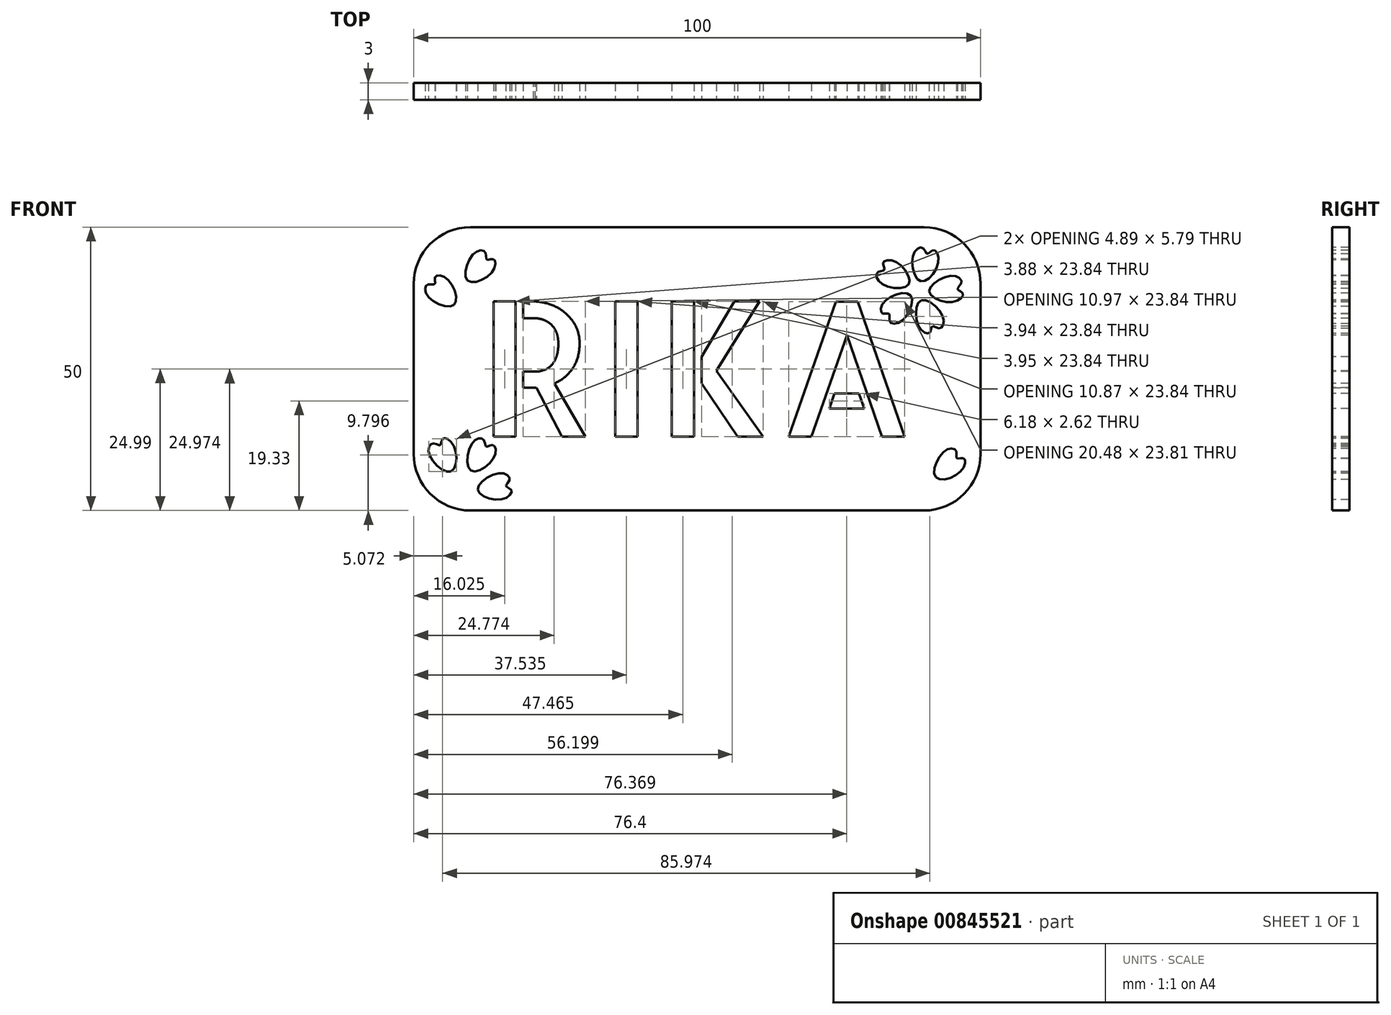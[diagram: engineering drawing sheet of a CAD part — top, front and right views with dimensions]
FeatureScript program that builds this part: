
annotation { "Feature Type Name" : "Feature", "Feature Type Description" : "" }
export const myFeature = defineFeature(function(context is Context, id is Id, definition is map)
    precondition{}
    {
        {
            var Q0;
            Q0=qCreatedBy(makeId("Front.planeOp"),FACE);
            var sketch = newSketch(context, id + "F0", { "sketchPlane" : qUnion([Q0])});
            skLineSegment(sketch, "E0.bottom", {"start": v(-50, 50) * mm, "end": v(50, 50) * mm});
            skLineSegment(sketch, "E0.top", {"start": v(-50, 0) * mm, "end": v(50, 0) * mm});
            skLineSegment(sketch, "E0.left", {"start": v(-50, 50) * mm, "end": v(-50, 0) * mm});
            skLineSegment(sketch, "E0.right", {"start": v(50, 50) * mm, "end": v(50, 0) * mm});
            skPoint(sketch, "E1", {"position": v(0, 0) * mm});
            skSolve(sketch);
        }
        {
            var Q0;
            Q0=qSketchRegion(id+"F0",true);
            extrude(context, id + "F1", {"entities" : qUnion([Q0]), "endBound" : BoundingType.SYMMETRIC, "depth" : 3 * mm, "offsetDistance" : 25 * mm});
        }
        {
            var Q0;
            Q0=makeQuery(id+"F1.opExtrude","SWEPT_EDGE",EDGE,{"disambiguationData":[OSD([sQuery(id+"F0.wireOp",EDGE,"E0.bottom"),sQuery(id+"F0.wireOp",EDGE,"E0.left")])]});
            var Q1;
            Q1=makeQuery(id+"F1.opExtrude","SWEPT_EDGE",EDGE,{"disambiguationData":[OSD([sQuery(id+"F0.wireOp",EDGE,"E0.bottom"),sQuery(id+"F0.wireOp",EDGE,"E0.right")])]});
            var Q2;
            Q2=makeQuery(id+"F1.opExtrude","SWEPT_EDGE",EDGE,{"disambiguationData":[OSD([sQuery(id+"F0.wireOp",EDGE,"E0.top"),sQuery(id+"F0.wireOp",EDGE,"E0.right")])]});
            var Q3;
            Q3=makeQuery(id+"F1.opExtrude","SWEPT_EDGE",EDGE,{"disambiguationData":[OSD([sQuery(id+"F0.wireOp",EDGE,"E0.top"),sQuery(id+"F0.wireOp",EDGE,"E0.left")])]});
            fillet(context, id + "F2", {"entities" : qUnion([Q0, Q1, Q2, Q3]), "radius" : 10 * mm, "tangentPropagation" : true, "allowEdgeOverflow" : false});
        }
        {
            var Q0;
            Q0=makeQuery(id+"F1.opExtrude","CAP_FACE",FACE,{"disambiguationData":[OSD([sQuery(id+"F0.wireOp",EDGE,"E0.bottom"),sQuery(id+"F0.wireOp",EDGE,"E0.top"),sQuery(id+"F0.wireOp",EDGE,"E0.left"),sQuery(id+"F0.wireOp",EDGE,"E0.right")])],"isStart":false});
            var sketch = newSketch(context, id + "F3", { "sketchPlane" : qUnion([Q0])});
            skText(sketch, "E2", { "text": "RIKA", "fontName": "AllertaStencil-Regular.ttf"});
            skPoint(sketch, "E3", {"position": v(-38.83, 25) * mm});
            const initialGuessF3  = {"E2": [-0.03883, 0.01307, 1, 0, 0.02385]};
            skSetInitialGuess(sketch, initialGuessF3);
            skSolve(sketch);
        }
        {
            var Q0;
            Q0=qSketchRegion(id+"F3",true);
            extrude(context, id + "F4", {"entities" : qUnion([Q0]), "operationType" : NewBodyOperationType.REMOVE, "oppositeDirection" : true, "depth" : 3 * mm, "offsetDistance" : 25 * mm});
        }
        {
            var Q0;
            Q0=makeQuery(id+"F1.opExtrude","CAP_FACE",FACE,{"disambiguationData":[OSD([sQuery(id+"F0.wireOp",EDGE,"E0.bottom"),sQuery(id+"F0.wireOp",EDGE,"E0.top"),sQuery(id+"F0.wireOp",EDGE,"E0.left"),sQuery(id+"F0.wireOp",EDGE,"E0.right")])],"isStart":false});
            var sketch = newSketch(context, id + "F5", { "sketchPlane" : qUnion([Q0])});
            skFitSpline(sketch, "E4", {"points": [v(39.43, 40.46) * mm, v(38.14, 45.22) * mm, v(39.8, 46.32) * mm, v(40.62, 45.31) * mm, v(41.63, 45.96) * mm, v(42.54, 43.94) * mm, v(39.43, 40.46) * mm]});
            skFitSpline(sketch, "E5", {"points": [v(37.31, 39.9) * mm, v(32.39, 40.14) * mm, v(31.85, 42.05) * mm, v(33.06, 42.52) * mm, v(32.77, 43.68) * mm, v(34.96, 43.93) * mm, v(37.31, 39.9) * mm]});
            skFitSpline(sketch, "E6", {"points": [v(37.68, 37.95) * mm, v(35.91, 33.34) * mm, v(33.93, 33.42) * mm, v(33.86, 34.72) * mm, v(32.67, 34.8) * mm, v(33.11, 36.96) * mm, v(37.68, 37.95) * mm]});
            skFitSpline(sketch, "E7", {"points": [v(39.58, 37.13) * mm, v(43.42, 34.03) * mm, v(42.73, 32.17) * mm, v(41.47, 32.5) * mm, v(41.03, 31.39) * mm, v(39.1, 32.48) * mm, v(39.58, 37.13) * mm]});
            skFitSpline(sketch, "E8", {"points": [v(40.94, 38.72) * mm, v(45.08, 41.42) * mm, v(46.63, 40.19) * mm, v(45.93, 39.1) * mm, v(46.85, 38.33) * mm, v(45.22, 36.84) * mm, v(40.94, 38.72) * mm]});
            skFitSpline(sketch, "E9", {"points": [v(-39.93, 7.08) * mm, v(-39.6, 12) * mm, v(-37.68, 12.5) * mm, v(-37.23, 11.28) * mm, v(-36.06, 11.56) * mm, v(-35.86, 9.36) * mm, v(-39.93, 7.08) * mm]});
            skFitSpline(sketch, "E10", {"points": [v(-43.46, 6.9) * mm, v(-47.3, 10) * mm, v(-46.61, 11.86) * mm, v(-45.35, 11.53) * mm, v(-44.91, 12.64) * mm, v(-43, 11.55) * mm, v(-43.46, 6.9) * mm]});
            skFitSpline(sketch, "E11", {"points": [v(-40.53, 40.61) * mm, v(-39.34, 45.4) * mm, v(-37.36, 45.57) * mm, v(-37.13, 44.28) * mm, v(-35.94, 44.36) * mm, v(-36.11, 42.15) * mm, v(-40.53, 40.61) * mm]});
            skFitSpline(sketch, "E12", {"points": [v(-42.92, 36.3) * mm, v(-47.59, 37.9) * mm, v(-47.58, 39.88) * mm, v(-46.28, 40) * mm, v(-46.25, 41.2) * mm, v(-44.07, 40.83) * mm, v(-42.92, 36.3) * mm]});
            skFitSpline(sketch, "E13", {"points": [v(42.1, 5.88) * mm, v(43.7, 10.55) * mm, v(45.68, 10.54) * mm, v(45.8, 9.24) * mm, v(47, 9.2) * mm, v(46.62, 7.03) * mm, v(42.1, 5.88) * mm]});
            skFitSpline(sketch, "E14", {"points": [v(-38.7, 3.7) * mm, v(-34.7, 6.6) * mm, v(-33.09, 5.46) * mm, v(-33.73, 4.33) * mm, v(-32.77, 3.61) * mm, v(-34.32, 2.04) * mm, v(-38.7, 3.7) * mm]});
            skSolve(sketch);
        }
        {
            var Q0;
            Q0=qSketchRegion(id+"F5",true);
            extrude(context, id + "F6", {"entities" : qUnion([Q0]), "operationType" : NewBodyOperationType.REMOVE, "oppositeDirection" : true, "depth" : 3 * mm, "offsetDistance" : 25 * mm});
        }
    });
